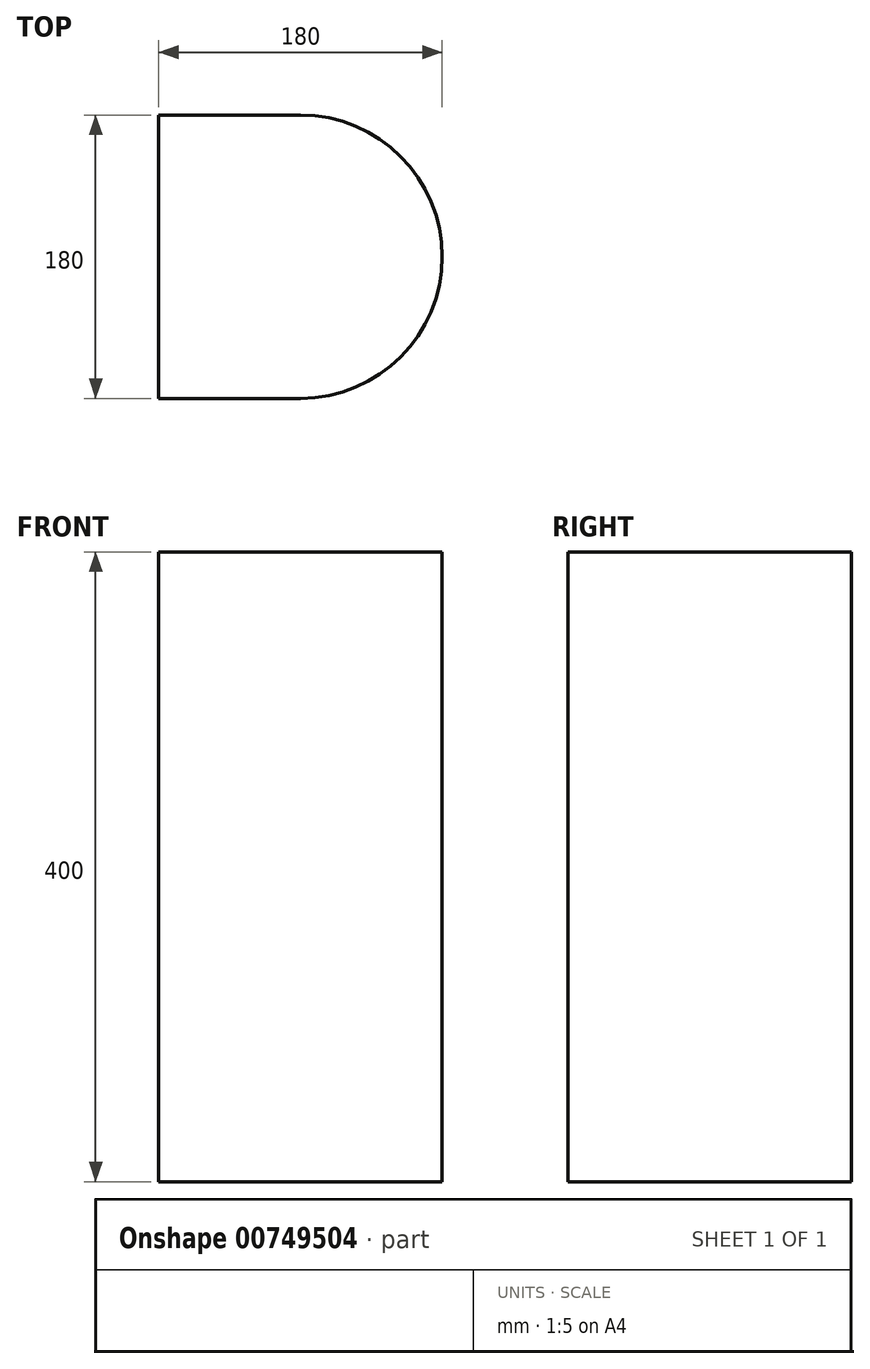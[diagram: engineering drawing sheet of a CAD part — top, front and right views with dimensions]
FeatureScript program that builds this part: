
annotation { "Feature Type Name" : "Feature", "Feature Type Description" : "" }
export const myFeature = defineFeature(function(context is Context, id is Id, definition is map)
    precondition{}
    {
        {
            var Q0;
            Q0=qCreatedBy(makeId("Top.planeOp"),FACE);
            var sketch = newSketch(context, id + "F0", { "sketchPlane" : qUnion([Q0])});
            skLineSegment(sketch, "E0", {"start": v(-47.7, 124.4) * mm, "end": v(-47.7, -55.6) * mm});
            skLineSegment(sketch, "E1", {"start": v(-47.7, 124.4) * mm, "end": v(42.3, 124.4) * mm});
            skLineSegment(sketch, "E2", {"start": v(-47.7, -55.6) * mm, "end": v(42.3, -55.6) * mm});
            skArc(sketch, "E3", {"start": v(42.3, -55.6) * mm, "mid": v(132.3, 34.4) * mm, "end": v(42.3, 124.4) * mm});
            skLineSegment(sketch, "E4", {"start": v(-183.9, 34.4) * mm, "end": v(96.4, 34.4) * mm, "construction": true});
            skLineSegment(sketch, "E5", {"start": v(42.3, 124.4) * mm, "end": v(42.3, -55.6) * mm, "construction": true});
            skSolve(sketch);
        }
        {
            var Q0;
            Q0=makeQuery(id+"F0.imprint","IMPRINT",FACE,{"disambiguationData":[TD([[makeQuery(id+"F0.imprint","IMPRINT",EDGE,{"derivedFrom":sQuery(id+"F0.wireOp",EDGE,"E0")}),1.0]])]});
            extrude(context, id + "F1", {"entities" : qUnion([Q0]), "depth" : 400 * mm, "offsetDistance" : 25 * mm});
        }
    });
